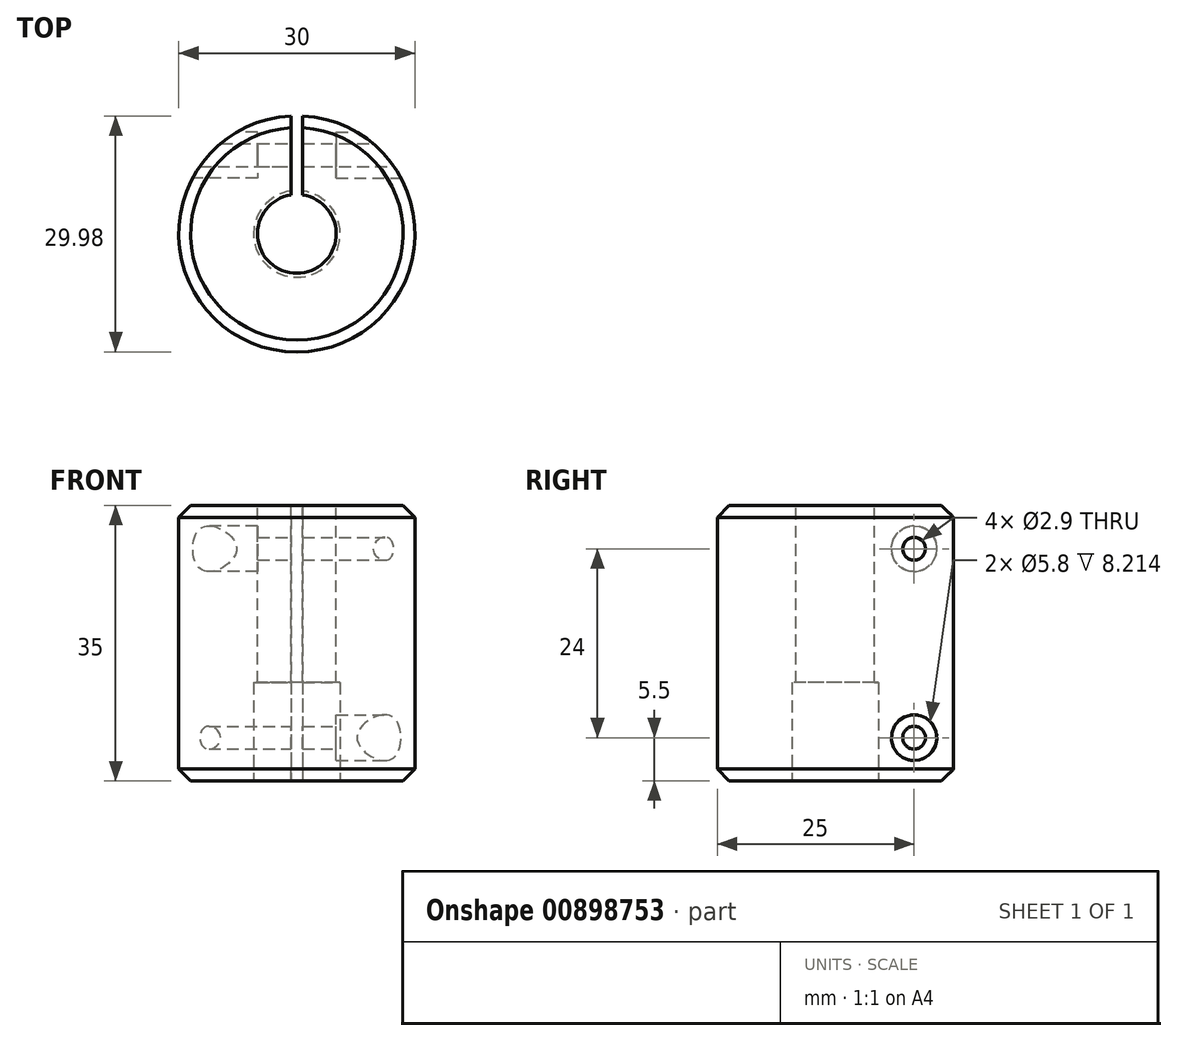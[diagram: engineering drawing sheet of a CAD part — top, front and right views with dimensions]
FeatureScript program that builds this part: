
annotation { "Feature Type Name" : "Feature", "Feature Type Description" : "" }
export const myFeature = defineFeature(function(context is Context, id is Id, definition is map)
    precondition{}
    {
        {
            var Q0;
            Q0=qCreatedBy(makeId("Top.planeOp"),FACE);
            var sketch = newSketch(context, id + "F0", { "sketchPlane" : qUnion([Q0])});
            skCircle(sketch, "E0", {"center": v(0, 0) * mm, "radius": 15 * mm});
            skSolve(sketch);
        }
        {
            var Q0;
            Q0 = qSketchRegion(id + "F0", true);
            extrude(context, id + "F1", {"entities" : qUnion([Q0]), "depth" : 35 * mm, "offsetDistance" : 25 * mm});
        }
        {
            var Q0;
            Q0=makeQuery(id+"F1.opExtrude","CAP_FACE",FACE,{"disambiguationData":[OSD([sQuery(id+"F0.wireOp",EDGE,"E0")])],"isStart":false});
            var sketch = newSketch(context, id + "F2", { "sketchPlane" : qUnion([Q0])});
            skCircle(sketch, "E1", {"center": v(0, 0) * mm, "radius": 5 * mm});
            skSolve(sketch);
        }
        {
            var Q0;
            Q0 = qSketchRegion(id + "F2", true);
            extrude(context, id + "F3", {"entities" : qUnion([Q0]), "operationType" : NewBodyOperationType.REMOVE, "endBound" : BoundingType.THROUGH_ALL, "oppositeDirection" : true, "depth" : 25 * mm, "offsetDistance" : 25 * mm});
        }
        {
            var Q0;
            Q0=makeQuery(id+"F1.opExtrude","CAP_FACE",FACE,{"disambiguationData":[OSD([sQuery(id+"F0.wireOp",EDGE,"E0")])],"isStart":true});
            var sketch = newSketch(context, id + "F4", { "sketchPlane" : qUnion([Q0])});
            skCircle(sketch, "E2", {"center": v(0, 0) * mm, "radius": 5.5 * mm});
            skSolve(sketch);
        }
        {
            var Q0;
            Q0 = qSketchRegion(id + "F4", true);
            extrude(context, id + "F5", {"entities" : qUnion([Q0]), "operationType" : NewBodyOperationType.REMOVE, "oppositeDirection" : true, "depth" : (25 / 2) * mm, "offsetDistance" : 25 * mm});
        }
        {
            var Q0;
            Q0=makeQuery(id+"F1.opExtrude","CAP_FACE",FACE,{"disambiguationData":[OSD([sQuery(id+"F0.wireOp",EDGE,"E0")])],"isStart":true});
            var sketch = newSketch(context, id + "F6", { "sketchPlane" : qUnion([Q0])});
            skLineSegment(sketch, "E3", {"start": v(0.75, 0) * mm, "end": v(0.75, -20) * mm});
            skLineSegment(sketch, "E4", {"start": v(0.75, -20) * mm, "end": v(-0.75, -20) * mm});
            skLineSegment(sketch, "E5", {"start": v(-0.75, -20) * mm, "end": v(-0.75, 0) * mm});
            skLineSegment(sketch, "E6", {"start": v(-0.75, 0) * mm, "end": v(0.75, 0) * mm});
            skSolve(sketch);
        }
        {
            var Q0;
            Q0 = qSketchRegion(id + "F6", true);
            extrude(context, id + "F7", {"entities" : qUnion([Q0]), "operationType" : NewBodyOperationType.REMOVE, "endBound" : BoundingType.THROUGH_ALL, "oppositeDirection" : true, "depth" : 25 * mm, "offsetDistance" : 25 * mm});
        }
        {
            var Q0;
            Q0=qCreatedBy(makeId("Right.planeOp"),FACE);
            var sketch = newSketch(context, id + "F8", { "sketchPlane" : qUnion([Q0])});
            skCircle(sketch, "E7", {"center": v(10, 5.5) * mm, "radius": 1.45 * mm});
            skCircle(sketch, "E8", {"center": v(10, 29.5) * mm, "radius": 1.45 * mm});
            skSolve(sketch);
        }
        {
            var Q0;
            Q0 = qSketchRegion(id + "F8", true);
            extrude(context, id + "F9", {"entities" : qUnion([Q0]), "operationType" : NewBodyOperationType.REMOVE, "endBound" : BoundingType.SYMMETRIC, "oppositeDirection" : true, "depth" : 25 * mm, "offsetDistance" : 25 * mm});
        }
        {
            var Q0;
            Q0=qCreatedBy(makeId("Right.planeOp"),FACE);
            cPlane(context, id + "F10", {"entities" : qUnion([Q0]), "cplaneType" : CPlaneType.OFFSET, "offset" : 15 * mm, "width" : 150 * mm, "height" : 150 * mm});
        }
        {
            var Q0;
            Q0=qCreatedBy(id+"F10.planeOp",FACE);
            var sketch = newSketch(context, id + "F11", { "sketchPlane" : qUnion([Q0])});
            skCircle(sketch, "E9", {"center": v(10, 5.5) * mm, "radius": 2.9 * mm});
            skSolve(sketch);
        }
        {
            var Q0;
            Q0 = qSketchRegion(id + "F11", true);
            extrude(context, id + "F12", {"entities" : qUnion([Q0]), "operationType" : NewBodyOperationType.REMOVE, "oppositeDirection" : true, "depth" : 10 * mm, "offsetDistance" : 25 * mm});
        }
        {
            var Q0;
            Q0=qCreatedBy(makeId("Right.planeOp"),FACE);
            cPlane(context, id + "F13", {"entities" : qUnion([Q0]), "cplaneType" : CPlaneType.OFFSET, "offset" : 15 * mm, "oppositeDirection" : true, "width" : 150 * mm, "height" : 150 * mm});
        }
        {
            var Q0;
            Q0=qCreatedBy(id+"F13.planeOp",FACE);
            var sketch = newSketch(context, id + "F14", { "sketchPlane" : qUnion([Q0])});
            skCircle(sketch, "E10", {"center": v(10, 29.5) * mm, "radius": 2.9 * mm});
            skSolve(sketch);
        }
        {
            var Q0;
            Q0 = qSketchRegion(id + "F14", true);
            extrude(context, id + "F15", {"entities" : qUnion([Q0]), "operationType" : NewBodyOperationType.REMOVE, "depth" : 10 * mm, "offsetDistance" : 25 * mm});
        }
        {
            var Q0;
            Q0=makeQuery(id+"F1.opExtrude","CAP_EDGE",EDGE,{"disambiguationData":[OSD([sQuery(id+"F0.wireOp",EDGE,"E0")])],"isStart":true});
            var Q1;
            Q1=makeQuery(id+"F1.opExtrude","CAP_EDGE",EDGE,{"disambiguationData":[OSD([sQuery(id+"F0.wireOp",EDGE,"E0")])],"isStart":false});
            chamfer(context, id + "F16", {"entities" : qUnion([Q0, Q1]), "width" : 1.5 * mm, "tangentPropagation" : true});
        }
    });
